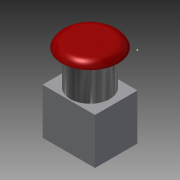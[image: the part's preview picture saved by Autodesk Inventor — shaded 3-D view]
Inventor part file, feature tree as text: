
AUTODESK INVENTOR PART (.ipt)
format: ipt  version: 2014 SP1 (Build 180222100, 222)  size: 110,592 bytes
history: native  units: in
note: dims shown in document units (in); Inventor stores cm internally (conversion verified against a paired STEP export)
features: sketch x4, extrude x3, fillet x1
ambient origin geometry x8: Origin, YZ Plane, XZ Plane, XY Plane, X Axis, Y Axis, Z Axis, Center Point
bodies: Solid1 (feature_tree)
feature tree (8):
  extrude  "Extrusion1"  Depth=1.177in
  extrude  "Extrusion2"  Depth=1.274in
  sketch  "Sketch3"  dims[d5=0.971in d6=0.0in d7=1.564in d8=0.187in d9=0.0in]
  extrude  "Extrusion3"  Depth=0.187in
  fillet  "Fillet1"  Radius=0.187in
  sketch  "Sketch1"  dims[d0=1.455in d1=1.177in]
  sketch  "Sketch2"  dims[d2=1.274in d3=0.0in d4=1.1in]
  sketch  "Sketch4"  dims[d10=0.3in]
